# Revit family: EDE-GRF-INS- TEMPO PREMIUM PARA URINARIO
name_source: partatom
category: Aparatos sanitarios
units: mm (PartAtom-declared; Revit-internal decimal feet)

## family parameters
Anfitrión = Muro
Compartido = No
Corte con vacíos al cargar = No
Cota de conector redondo = Diámetro de uso
Número OmniClass = 23.45.00.00
Punto de cálculo de habitación = No
Siempre vertical = Sí
Tipo de pieza = Normal
Título OmniClass = Sanitary, Laundry, and Cleaning Equipment

## types (1)
- TEMPO PREMIUM PARA URINARIO
    Elevación por defecto = 0 m
    Fabricante = EDESA-PREMIUM ECUADOR
    Modelo = TEMPO PREMIUM PARA URINARIO
    URL = https://www.edesa.com.ec
    _ALT_Base inodoro = 0.4 m
    _EDESA_ Alto en cm = 22.5
    _EDESA_ Ancho en cm = 5.4
    _EDESA_ Certificación = Cumple con la norma ASSE 1037 (Pressurized Flushing Devices - Flushometers - for Plumbing Fixtures)
    _EDESA_ Color = Cromo
    _EDESA_ Conexión hidráulica = Entrada de agua: tubería ø 1/2"
    _EDESA_ Consumo/capacidad de agua en L = 1.2 litros por descarga
    _EDESA_ Descripción = Llave temporizada para urinario. Instalación a la pared
    _EDESA_ Nombre = TEMPO PREMIUM PARA URINARIO
    _EDESA_ Productos incluídos = Cobertor para la pared y spud
    _EDESA_ Profundidad en cm = 11.6
    _EDESA_ Sku/código = SG0057833061CE
    _EDESA_ Tipo de instalación = A la pared
    _EDESA_Categoria = Productos > Griferia > Institucional
    _EDESA_Garantia = De por vida para el cuerpo principal y acabado en cromo (306)
    _EDESA_Material = Latón
